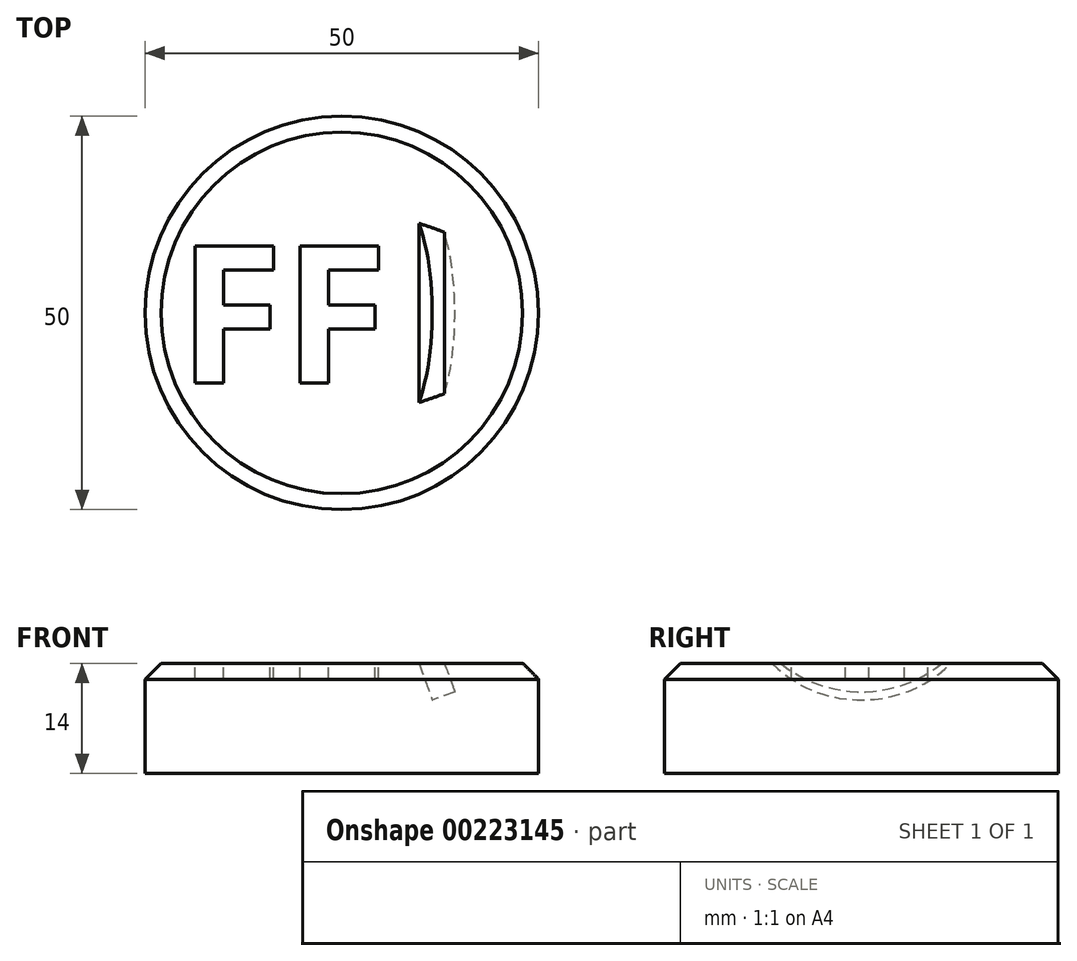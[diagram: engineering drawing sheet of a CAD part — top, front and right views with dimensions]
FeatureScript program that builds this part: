
annotation { "Feature Type Name" : "Feature", "Feature Type Description" : "" }
export const myFeature = defineFeature(function(context is Context, id is Id, definition is map)
    precondition{}
    {
        {
            var Q0;
            Q0=qCreatedBy(makeId("Top.planeOp"),FACE);
            var sketch = newSketch(context, id + "F0", { "sketchPlane" : qUnion([Q0])});
            skCircle(sketch, "E0", {"center": v(0, 0) * mm, "radius": 25 * mm});
            skSolve(sketch);
        }
        {
            var Q0;
            Q0 = qSketchRegion(id + "F0", true);
            extrude(context, id + "F1", {"entities" : qUnion([Q0]), "depth" : 14 * mm});
        }
        {
            var Q0;
            Q0=qCreatedBy(makeId("Front.planeOp"),FACE);
            var sketch = newSketch(context, id + "F2", { "sketchPlane" : qUnion([Q0])});
            skLineSegment(sketch, "E1", {"start": v(16.51, 0) * mm, "end": v(6.36, 27.89) * mm});
            skSolve(sketch);
        }
        {
            var Q0;
            Q0=sQuery(id+"F2.wireOp",EDGE,"E1");
            cPlane(context, id + "F3", {"entities" : qUnion([Q0]), "cplaneType" : CPlaneType.LINE_ANGLE, "offset" : 25.4 * mm, "angle" : 0 * degree, "width" : 152.4 * mm, "height" : 152.4 * mm});
        }
        {
            var Q0;
            Q0=qCreatedBy(id+"F3.planeOp",FACE);
            var sketch = newSketch(context, id + "F4", { "sketchPlane" : qUnion([Q0])});
            skCircle(sketch, "E2", {"center": v(0, 20.32) * mm, "radius": 15.5 * mm});
            skLineSegment(sketch, "E3", {"start": v(-17.9, 0) * mm, "end": v(18.52, 0) * mm, "construction": true});
            skSolve(sketch);
        }
        {
            var Q0;
            Q0 = qSketchRegion(id + "F4", true);
            extrude(context, id + "F5", {"entities" : qUnion([Q0]), "operationType" : NewBodyOperationType.REMOVE, "endBound" : BoundingType.SYMMETRIC, "depth" : 3.05 * mm});
        }
        {
            var Q0;
            Q0=makeQuery(id+"F1.opExtrude","CAP_FACE",FACE,{"disambiguationData":[OSD([sQuery(id+"F0.wireOp",EDGE,"E0")])],"isStart":false});
            var sketch = newSketch(context, id + "F6", { "sketchPlane" : qUnion([Q0])});
            skText(sketch, "E4", { "text": "FF", "fontName": "OpenSans-Bold.ttf"});
            const initialGuessF6  = {"E4": [-0.02083, -0.0089, 1, 0, 0.01753]};
            skSetInitialGuess(sketch, initialGuessF6);
            skSolve(sketch);
        }
        {
            var Q0;
            Q0 = qSketchRegion(id + "F6", true);
            extrude(context, id + "F7", {"entities" : qUnion([Q0]), "operationType" : NewBodyOperationType.REMOVE, "oppositeDirection" : true, "depth" : 2.03 * mm});
        }
        {
            var Q0;
            Q0=makeQuery(id+"F1.opExtrude","CAP_EDGE",EDGE,{"disambiguationData":[OSD([sQuery(id+"F0.wireOp",EDGE,"E0")])],"isStart":false});
            chamfer(context, id + "F8", {"entities" : qUnion([Q0]), "width" : 2.03 * mm, "tangentPropagation" : true});
        }
    });
